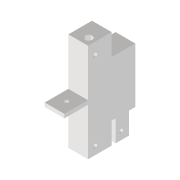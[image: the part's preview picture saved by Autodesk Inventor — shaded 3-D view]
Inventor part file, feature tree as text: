
AUTODESK INVENTOR PART (.ipt)
format: ipt  version: 2022 (Build 260153000, 153)  size: 136,192 bytes
history: native  units: mm
features: extrude x3, sketch x3, projected_geometry x2
ambient origin geometry x8: Origin, YZ Plane, XZ Plane, XY Plane, X Axis, Y Axis, Z Axis, Center Point
bodies: Solid1 (feature_tree)
feature tree (8):
  extrude  "Extrusion1"  Depth=6.0mm
  extrude  "Extrusion2"  Depth=1.0mm
  extrude  "Extrusion3"  Depth=10.0mm
  sketch  "Sketch1"  dims[d0=25.0mm d1=6.0mm]
  sketch  "Sketch2"  dims[d2=1.0mm d3=1.0mm]
  projected_geometry  "Projected Loop1"
  sketch  "Skizze3"  dims[d4=20.0mm d5=14.0mm d6=6.0mm d8=1.0mm d9=6.0mm d10=10.0mm d11=5.0mm d12=0.0mm d13=2.0mm d14=1.0mm d15=5.0mm d16=0.0mm d18=3.0mm d19=5.5mm d20=1.0mm d21=6.6mm d22=10.0mm d23=0.0mm]
  projected_geometry  "Projizierte Kontur2"
